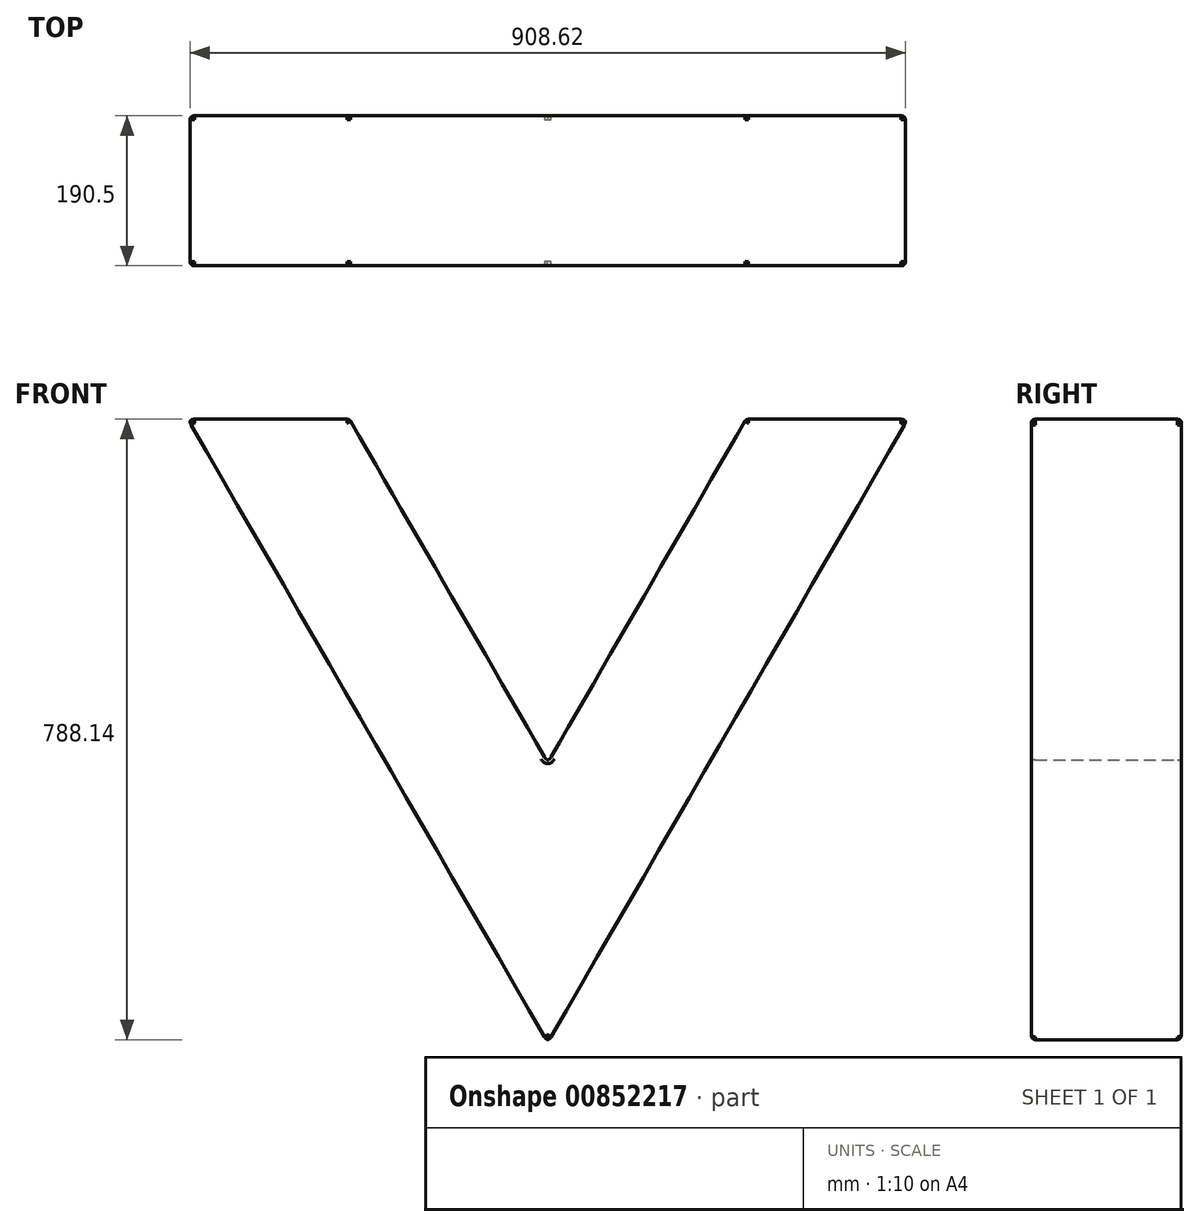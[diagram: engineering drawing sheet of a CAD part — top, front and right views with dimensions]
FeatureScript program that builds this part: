
annotation { "Feature Type Name" : "Feature", "Feature Type Description" : "" }
export const myFeature = defineFeature(function(context is Context, id is Id, definition is map)
    precondition{}
    {
        {
            var Q0;
            Q0=qCreatedBy(makeId("Front.planeOp"),FACE);
            var sketch = newSketch(context, id + "F0", { "sketchPlane" : qUnion([Q0])});
            skLineSegment(sketch, "E0", {"start": v(0, 0) * mm, "end": v(457.2, 791.9) * mm});
            skLineSegment(sketch, "E1", {"start": v(457.2, 791.9) * mm, "end": v(251.9, 791.9) * mm});
            skLineSegment(sketch, "E2", {"start": v(251.9, 791.9) * mm, "end": v(0, 355.6) * mm});
            skLineSegment(sketch, "E3", {"start": v(0, 355.6) * mm, "end": v(0, 0) * mm, "construction": true});
            skLineSegment(sketch, "E4.MirrorCS", {"start": v(-251.9, 791.9) * mm, "end": v(0, 355.6) * mm});
            skLineSegment(sketch, "E5.MirrorCS", {"start": v(-457.2, 791.9) * mm, "end": v(-251.9, 791.9) * mm});
            skLineSegment(sketch, "E6.MirrorCS", {"start": v(0, 0) * mm, "end": v(-457.2, 791.9) * mm});
            skSolve(sketch);
        }
        {
            var Q0;
            Q0 = qSketchRegion(id + "F0", true);
            extrude(context, id + "F1", {"entities" : qUnion([Q0]), "endBound" : BoundingType.SYMMETRIC, "depth" : 190.5 * mm, "offsetDistance" : 25 * mm});
        }
        {
            var Q0;
            Q0=makeQuery(id+"F1.opExtrude","CAP_FACE",FACE,{"disambiguationData":[OSD([sQuery(id+"F0.wireOp",EDGE,"E0"),sQuery(id+"F0.wireOp",EDGE,"E1"),sQuery(id+"F0.wireOp",EDGE,"E2"),sQuery(id+"F0.wireOp",EDGE,"E4.MirrorCS"),sQuery(id+"F0.wireOp",EDGE,"E5.MirrorCS"),sQuery(id+"F0.wireOp",EDGE,"E6.MirrorCS")])],"isStart":false});
            var Q1;
            Q1=makeQuery(id+"F1.opExtrude","CAP_FACE",FACE,{"disambiguationData":[OSD([sQuery(id+"F0.wireOp",EDGE,"E0"),sQuery(id+"F0.wireOp",EDGE,"E1"),sQuery(id+"F0.wireOp",EDGE,"E2"),sQuery(id+"F0.wireOp",EDGE,"E4.MirrorCS"),sQuery(id+"F0.wireOp",EDGE,"E5.MirrorCS"),sQuery(id+"F0.wireOp",EDGE,"E6.MirrorCS")])],"isStart":true});
            var Q2;
            Q2=makeQuery(id+"F1.opExtrude","SWEPT_EDGE",EDGE,{"disambiguationData":[OSD([sQuery(id+"F0.wireOp",EDGE,"E4.MirrorCS"),sQuery(id+"F0.wireOp",EDGE,"E5.MirrorCS")])]});
            var Q3;
            Q3=makeQuery(id+"F1.opExtrude","SWEPT_EDGE",EDGE,{"disambiguationData":[OSD([sQuery(id+"F0.wireOp",EDGE,"E1"),sQuery(id+"F0.wireOp",EDGE,"E2")])]});
            var Q4;
            Q4=makeQuery(id+"F1.opExtrude","SWEPT_EDGE",EDGE,{"disambiguationData":[OSD([sQuery(id+"F0.wireOp",EDGE,"E0"),sQuery(id+"F0.wireOp",EDGE,"E1")])]});
            var Q5;
            Q5=makeQuery(id+"F1.opExtrude","SWEPT_EDGE",EDGE,{"disambiguationData":[OSD([sQuery(id+"F0.wireOp",EDGE,"E0"),sQuery(id+"F0.wireOp",EDGE,"E6.MirrorCS")])]});
            var Q6;
            Q6=makeQuery(id+"F1.opExtrude","SWEPT_EDGE",EDGE,{"disambiguationData":[OSD([sQuery(id+"F0.wireOp",EDGE,"E2"),sQuery(id+"F0.wireOp",EDGE,"E4.MirrorCS")])]});
            var Q7;
            Q7=makeQuery(id+"F1.opExtrude","SWEPT_EDGE",EDGE,{"disambiguationData":[OSD([sQuery(id+"F0.wireOp",EDGE,"E5.MirrorCS"),sQuery(id+"F0.wireOp",EDGE,"E6.MirrorCS")])]});
            fillet(context, id + "F2", {"entities" : qUnion([Q0, Q1, Q2, Q3, Q4, Q5, Q6, Q7]), "radius" : 5 * mm, "tangentPropagation" : true, "rho" : 0.5, "crossSection" : FilletCrossSection.CONIC, "allowEdgeOverflow" : false});
        }
    });
